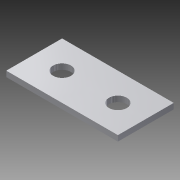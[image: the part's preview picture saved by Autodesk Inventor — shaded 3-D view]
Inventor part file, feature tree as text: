
AUTODESK INVENTOR PART (.ipt)
format: ipt  version: 2015 (Build 190159000, 159)  size: 102,400 bytes
history: native  units: mm
features: sketch x2, other x1, extrude x1, hole x1
ambient origin geometry x8: Origin, YZ Plane, XZ Plane, XY Plane, X Axis, Y Axis, Z Axis, Center Point
bodies: Body1 (feature_tree)
feature tree (5):
  other  "ソリッド1"
  extrude  "押し出し1"  Depth=20.0mm
  hole  "穴1"  [1 undecoded]
  sketch  "スケッチ1"
  sketch  "スケッチ2"
note: 1 required parameter value undecoded (feature->parameter linkage not recoverable at this tier; creation-order binding heuristic only, values carry confidence <= 0.55)
